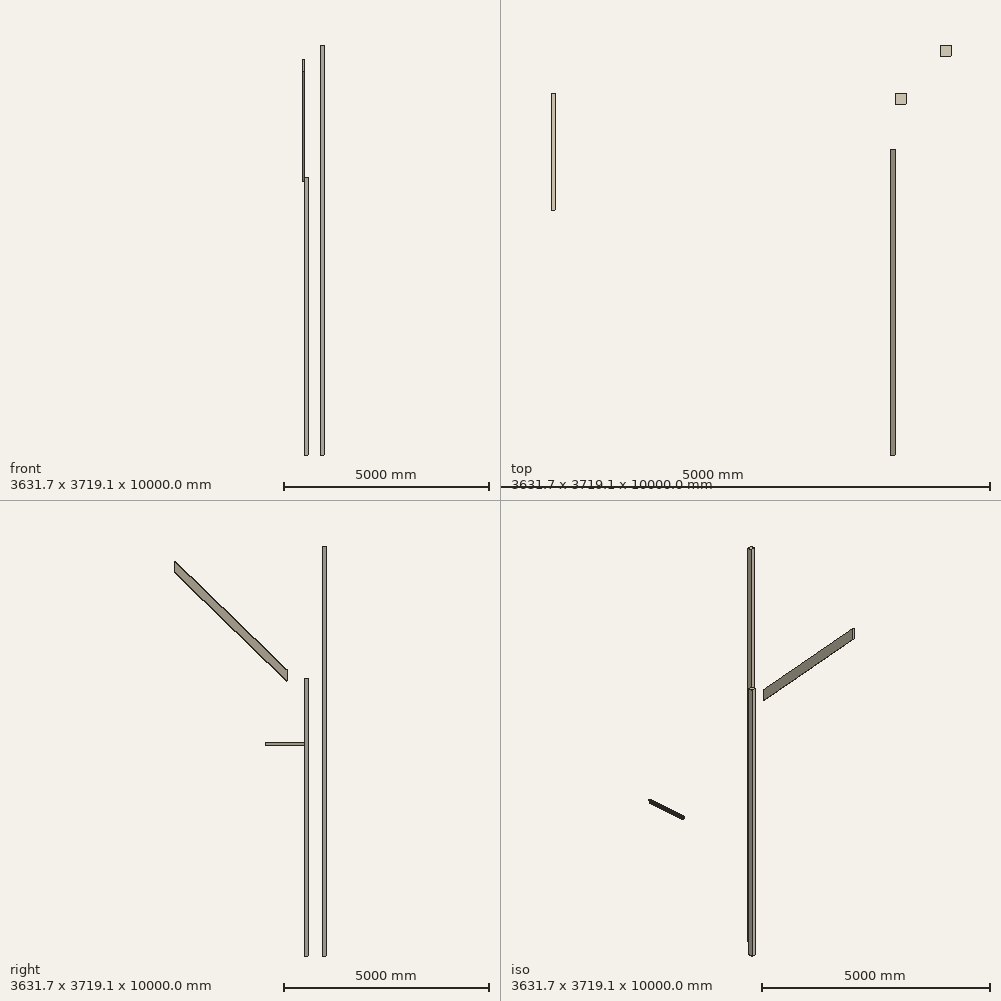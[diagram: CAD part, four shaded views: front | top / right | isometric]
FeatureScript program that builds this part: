
annotation { "Feature Type Name" : "Feature", "Feature Type Description" : "" }
export const myFeature = defineFeature(function(context is Context, id is Id, definition is map)
    precondition{}
    {
        {
            var Q0;
            Q0=qCreatedBy(makeId("Top.planeOp"),FACE);
            var sketch = newSketch(context, id + "F0", { "sketchPlane" : qUnion([Q0])});
            skLineSegment(sketch, "E0.bottom", {"start": v(-82.28, -97.19) * mm, "end": v(17.72, -97.19) * mm});
            skLineSegment(sketch, "E0.top", {"start": v(-82.28, 2.81) * mm, "end": v(17.72, 2.81) * mm});
            skLineSegment(sketch, "E0.left", {"start": v(-82.28, -97.19) * mm, "end": v(-82.28, 2.81) * mm});
            skLineSegment(sketch, "E0.right", {"start": v(17.72, -97.19) * mm, "end": v(17.72, 2.81) * mm});
            skSolve(sketch);
        }
        {
            var Q0;
            Q0=makeQuery(id+"F0.imprint","IMPRINT",FACE,{"disambiguationData":[TD([[makeQuery(id+"F0.imprint","IMPRINT",EDGE,{"derivedFrom":sQuery(id+"F0.wireOp",EDGE,"E0.bottom")}),1.0]])]});
            extrude(context, id + "F1", {"entities" : qUnion([Q0]), "depth" : 6770 * mm});
        }
        {
            var Q0;
            Q0=makeQuery(id+"F1.opExtrude","SWEPT_FACE",FACE,{"disambiguationData":[OSD([sQuery(id+"F0.wireOp",EDGE,"E0.left")])]});
            var sketch = newSketch(context, id + "F2", { "sketchPlane" : qUnion([Q0])});
            skLineSegment(sketch, "E1", {"start": v(506.77, 6687.96) * mm, "end": v(506.77, 6966.43) * mm});
            skLineSegment(sketch, "E2", {"start": v(506.77, 6966.43) * mm, "end": v(3279.08, 9652.3) * mm});
            skLineSegment(sketch, "E3", {"start": v(3279.08, 9652.3) * mm, "end": v(3279.08, 9373.83) * mm});
            skLineSegment(sketch, "E4.0", {"start": v(506.77, 6687.96) * mm, "end": v(3279.08, 9373.83) * mm});
            skSolve(sketch);
        }
        {
            var Q0;
            Q0=makeQuery(id+"F2.imprint","IMPRINT",FACE,{"disambiguationData":[TD([[makeQuery(id+"F2.imprint","IMPRINT",EDGE,{"derivedFrom":sQuery(id+"F2.wireOp",EDGE,"E1")}),-1.0]])]});
            extrude(context, id + "F3", {"entities" : qUnion([Q0]), "depth" : 50 * mm});
        }
        {
            var Q0;
            Q0=qCreatedBy(makeId("Front.planeOp"),FACE);
            var sketch = newSketch(context, id + "F4", { "sketchPlane" : qUnion([Q0])});
            skLineSegment(sketch, "E5", {"start": v(-3208.29, 5212.55) * mm, "end": v(-3166.29, 5212.55) * mm});
            skLineSegment(sketch, "E6", {"start": v(-3166.29, 5212.55) * mm, "end": v(-3166.29, 5147.55) * mm});
            skLineSegment(sketch, "E7", {"start": v(-3166.29, 5147.55) * mm, "end": v(-3208.29, 5147.55) * mm});
            skLineSegment(sketch, "E8.0", {"start": v(-3171.29, 5207.55) * mm, "end": v(-3171.29, 5152.55) * mm});
            skLineSegment(sketch, "E9", {"start": v(-3208.29, 5212.55) * mm, "end": v(-3208.29, 5210.55) * mm});
            skLineSegment(sketch, "E10", {"start": v(-3208.29, 5147.55) * mm, "end": v(-3208.29, 5149.55) * mm});
            skLineSegment(sketch, "E11", {"start": v(-3208.29, 5210.55) * mm, "end": v(-3171.29, 5207.55) * mm});
            skLineSegment(sketch, "E12", {"start": v(-3208.29, 5149.55) * mm, "end": v(-3171.29, 5152.55) * mm});
            skSolve(sketch);
        }
        {
            var Q0;
            Q0=makeQuery(id+"F4.imprint","IMPRINT",FACE,{"disambiguationData":[TD([[makeQuery(id+"F4.imprint","IMPRINT",EDGE,{"derivedFrom":sQuery(id+"F4.wireOp",EDGE,"E5")}),-1.0]])]});
            extrude(context, id + "F5", {"entities" : qUnion([Q0]), "depth" : 1060 * mm});
        }
        {
            var Q0;
            Q0=qCreatedBy(makeId("Top.planeOp"),FACE);
            var sketch = newSketch(context, id + "F6", { "sketchPlane" : qUnion([Q0])});
            skLineSegment(sketch, "E13.bottom", {"start": v(323.42, 340.02) * mm, "end": v(423.42, 340.02) * mm});
            skLineSegment(sketch, "E13.top", {"start": v(323.42, 440.02) * mm, "end": v(423.42, 440.02) * mm});
            skLineSegment(sketch, "E13.left", {"start": v(323.42, 340.02) * mm, "end": v(323.42, 440.02) * mm});
            skLineSegment(sketch, "E13.right", {"start": v(423.42, 340.02) * mm, "end": v(423.42, 440.02) * mm});
            skSolve(sketch);
        }
        {
            var Q0;
            Q0 = qSketchRegion(id + "F6", true);
            extrude(context, id + "F7", {"entities" : qUnion([Q0]), "depth" : 10000 * mm});
        }
    });
